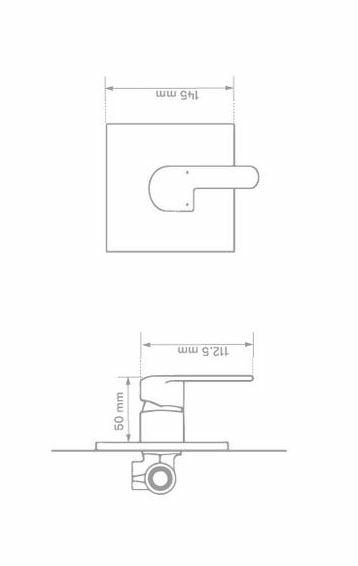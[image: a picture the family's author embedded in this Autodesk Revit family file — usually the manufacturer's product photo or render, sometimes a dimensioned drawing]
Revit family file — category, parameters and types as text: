
# Revit family: 01-1135-00SR-MEZCLADOR SST KRISTHAL
name_source: partatom
category: Aparatos sanitarios
revit_build: Autodesk Revit 2018 (Build: 20170223_1515(x64)
units: mm (PartAtom-declared; Revit-internal decimal feet)

## family parameters
Anfitrión = Cara
Compartido = No
Corte con vacíos al cargar = No
Cota de conector redondo = Diámetro de uso
Número OmniClass = 23.31.11.00
Punto de cálculo de habitación = No
Tipo de pieza = Normal

## types (1)
- 01-1135-00SR
    Alto = 60 mm  [stored 0.19685 ft]
    Ancho = 60 mm  [stored 0.19685 ft]
    Conexión AC = Sí
    Conexión AF = Sí
    Conexión de residuos = No
    Conexión de ventilación = No
    Descripción = Mezclador ducha
    Distancia entre griferias = 203 mm
    Elevación por defecto = 0 mm  [stored 0 ft]
    Fabricante = Gricol
    Imagen de tipo = <Ninguno>
    Link Ficha Tecnica = https://infotecnica.gricol.com
    Modelo = 01-1135-00SR
    Plastico ABS Cromado = Plastico ABS Cromado
    Plastico Acrilico Transparente = Plastico Acrilico Transparente
    Product Name = MEZCLADOR 8 SST KRISTHAL
    Profundidad = 85 mm  [stored 0.278871 ft]
    URL = https://www.gricol.com

note: [stored X ft] marks values corroborated as IEEE doubles in the binary element streams (Revit-internal decimal feet)

## geometry (parser evidence)
native form markers: Blend x2, Sweep x8
no freeform markers — native parametric forms only
